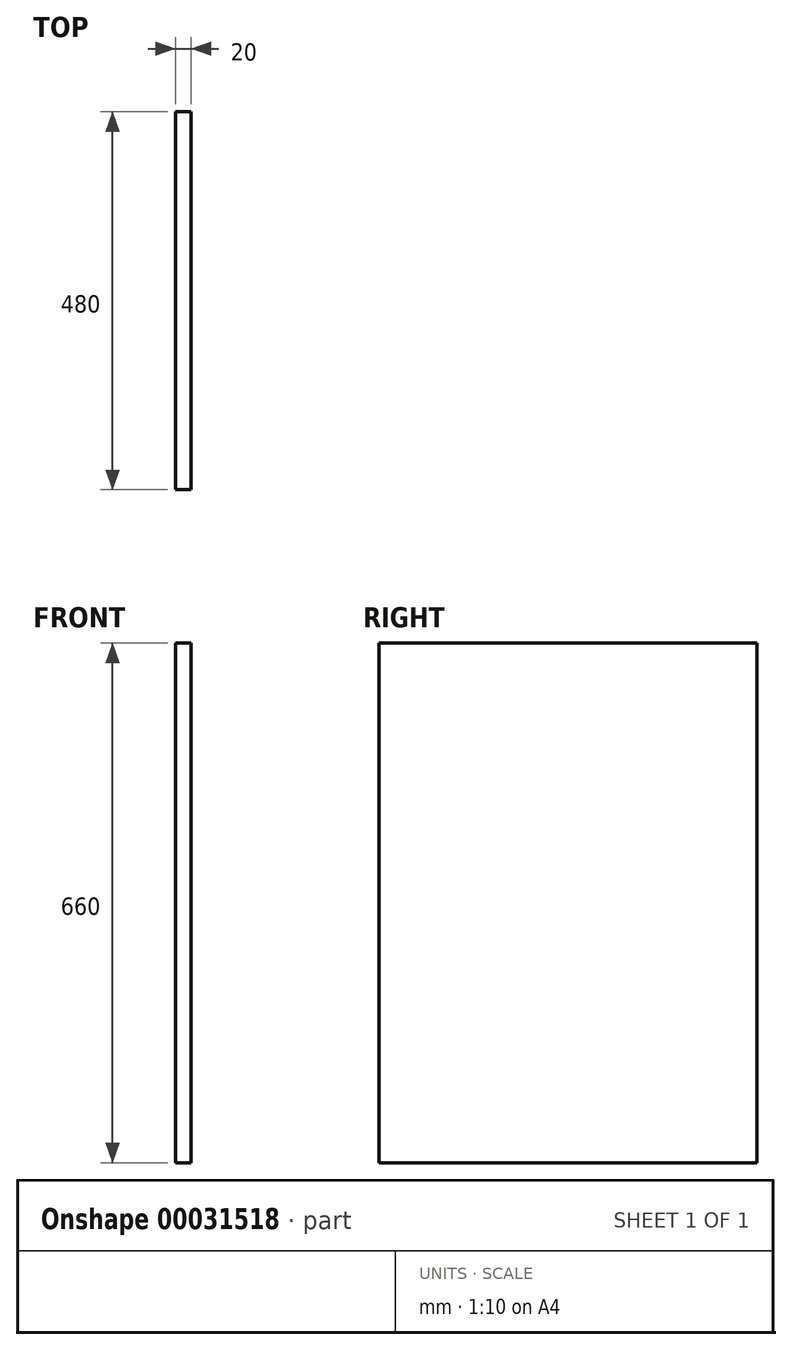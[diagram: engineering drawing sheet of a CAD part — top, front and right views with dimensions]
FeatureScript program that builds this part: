
annotation { "Feature Type Name" : "Feature", "Feature Type Description" : "" }
export const myFeature = defineFeature(function(context is Context, id is Id, definition is map)
    precondition{}
    {
        {
            var Q0;
            Q0=qCreatedBy(makeId("Front.planeOp"),FACE);
            var sketch = newSketch(context, id + "F0", { "sketchPlane" : qUnion([Q0])});
            skLineSegment(sketch, "E0.bottom", {"start": v(34.16, 504.4) * mm, "end": v(54.16, 504.4) * mm});
            skLineSegment(sketch, "E0.top", {"start": v(34.16, -155.6) * mm, "end": v(54.16, -155.6) * mm});
            skLineSegment(sketch, "E0.left", {"start": v(34.16, 504.4) * mm, "end": v(34.16, -155.6) * mm});
            skLineSegment(sketch, "E0.right", {"start": v(54.16, 504.4) * mm, "end": v(54.16, -155.6) * mm});
            skSolve(sketch);
        }
        {
            var Q0;
            Q0=makeQuery(id+"F0.imprint","IMPRINT",FACE,{"disambiguationData":[TD([[makeQuery(id+"F0.imprint","IMPRINT",EDGE,{"derivedFrom":sQuery(id+"F0.wireOp",EDGE,"E0.bottom")}),-1.0]])]});
            extrude(context, id + "F1", {"entities" : qUnion([Q0]), "oppositeDirection" : true, "depth" : 480 * mm});
        }
    });
